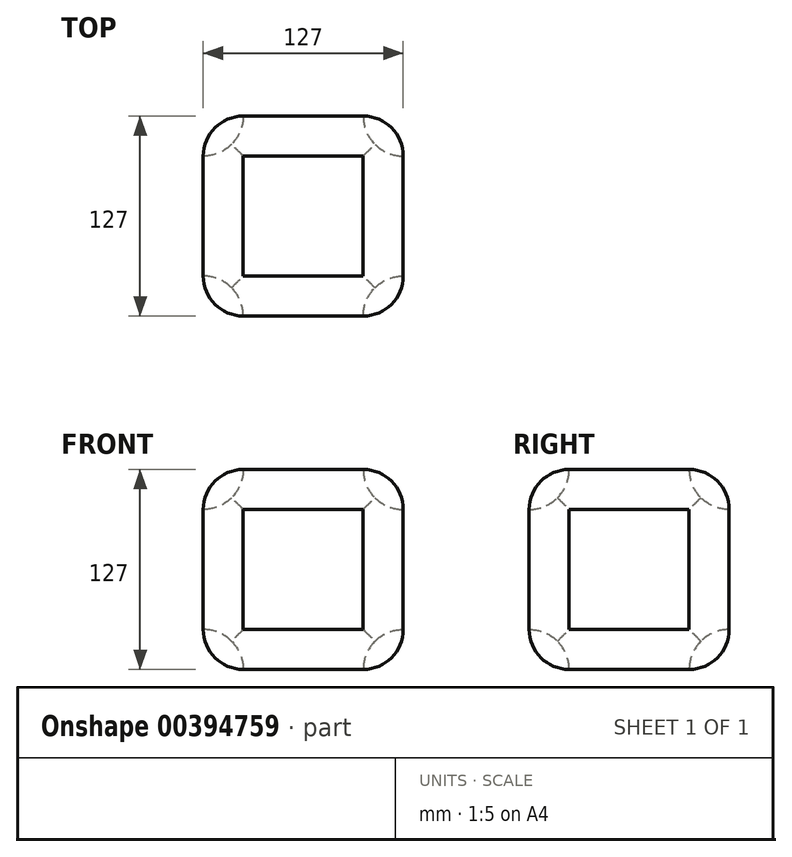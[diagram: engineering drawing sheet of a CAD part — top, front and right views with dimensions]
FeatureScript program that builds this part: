
annotation { "Feature Type Name" : "Feature", "Feature Type Description" : "" }
export const myFeature = defineFeature(function(context is Context, id is Id, definition is map)
    precondition{}
    {
        {
            var Q0;
            Q0=qCreatedBy(makeId("Front.planeOp"),FACE);
            var sketch = newSketch(context, id + "F0", { "sketchPlane" : qUnion([Q0])});
            skLineSegment(sketch, "E0.bottom", {"start": v(0, 0) * mm, "end": v(-127, 0) * mm});
            skLineSegment(sketch, "E0.top", {"start": v(0, -127) * mm, "end": v(-127, -127) * mm});
            skLineSegment(sketch, "E0.left", {"start": v(0, 0) * mm, "end": v(0, -127) * mm});
            skLineSegment(sketch, "E0.right", {"start": v(-127, 0) * mm, "end": v(-127, -127) * mm});
            skSolve(sketch);
        }
        {
            var Q0;
            Q0=makeQuery(id+"F0.imprint","IMPRINT",FACE,{"disambiguationData":[TD([[makeQuery(id+"F0.imprint","IMPRINT",EDGE,{"derivedFrom":sQuery(id+"F0.wireOp",EDGE,"E0.bottom")}),1.0]])]});
            extrude(context, id + "F1", {"entities" : qUnion([Q0]), "depth" : 127 * mm});
        }
        {
            var Q0;
            Q0=makeQuery(id+"F1.opExtrude","CAP_FACE",FACE,{"disambiguationData":[OSD([sQuery(id+"F0.wireOp",EDGE,"E0.bottom"),sQuery(id+"F0.wireOp",EDGE,"E0.top"),sQuery(id+"F0.wireOp",EDGE,"E0.left"),sQuery(id+"F0.wireOp",EDGE,"E0.right")])],"isStart":false});
            var sketch = newSketch(context, id + "F2", { "sketchPlane" : qUnion([Q0])});
            skLineSegment(sketch, "E1.bottom", {"start": v(-101.6, -25.4) * mm, "end": v(-25.4, -25.4) * mm});
            skLineSegment(sketch, "E1.top", {"start": v(-101.6, -101.6) * mm, "end": v(-25.4, -101.6) * mm});
            skLineSegment(sketch, "E1.left", {"start": v(-101.6, -25.4) * mm, "end": v(-101.6, -101.6) * mm});
            skLineSegment(sketch, "E1.right", {"start": v(-25.4, -25.4) * mm, "end": v(-25.4, -101.6) * mm});
            skSolve(sketch);
        }
        {
            var Q0;
            Q0=makeQuery(id+"F2.imprint","IMPRINT",FACE,{"disambiguationData":[TD([[makeQuery(id+"F2.imprint","IMPRINT",EDGE,{"derivedFrom":sQuery(id+"F2.wireOp",EDGE,"E1.bottom")}),-1.0]])]});
            var Q1;
            Q1=makeQuery(id+"F1.opExtrude","CAP_FACE",FACE,{"disambiguationData":[OSD([sQuery(id+"F0.wireOp",EDGE,"E0.bottom"),sQuery(id+"F0.wireOp",EDGE,"E0.top"),sQuery(id+"F0.wireOp",EDGE,"E0.left"),sQuery(id+"F0.wireOp",EDGE,"E0.right")])],"isStart":true});
            extrude(context, id + "F3", {"entities" : qUnion([Q0]), "operationType" : NewBodyOperationType.REMOVE, "endBound" : BoundingType.THROUGH_ALL, "oppositeDirection" : true, "endBoundEntityFace" : qUnion([Q1]), "depth" : 50.8 * mm});
        }
        {
            var Q0;
            Q0=makeQuery(id+"F1.opExtrude","SWEPT_FACE",FACE,{"disambiguationData":[OSD([sQuery(id+"F0.wireOp",EDGE,"E0.bottom")])]});
            var sketch = newSketch(context, id + "F4", { "sketchPlane" : qUnion([Q0])});
            skLineSegment(sketch, "E2.bottom", {"start": v(-101.6, -101.6) * mm, "end": v(-25.4, -101.6) * mm});
            skLineSegment(sketch, "E2.top", {"start": v(-101.6, -25.4) * mm, "end": v(-25.4, -25.4) * mm});
            skLineSegment(sketch, "E2.left", {"start": v(-101.6, -101.6) * mm, "end": v(-101.6, -25.4) * mm});
            skLineSegment(sketch, "E2.right", {"start": v(-25.4, -101.6) * mm, "end": v(-25.4, -25.4) * mm});
            skSolve(sketch);
        }
        {
            var Q0;
            Q0=makeQuery(id+"F4.imprint","IMPRINT",FACE,{"disambiguationData":[TD([[makeQuery(id+"F4.imprint","IMPRINT",EDGE,{"derivedFrom":sQuery(id+"F4.wireOp",EDGE,"E2.bottom")}),1.0]])]});
            extrude(context, id + "F5", {"entities" : qUnion([Q0]), "operationType" : NewBodyOperationType.REMOVE, "endBound" : BoundingType.THROUGH_ALL, "oppositeDirection" : true, "depth" : 25.4 * mm});
        }
        {
            var Q0;
            Q0=makeQuery(id+"F1.opExtrude","SWEPT_FACE",FACE,{"disambiguationData":[OSD([sQuery(id+"F0.wireOp",EDGE,"E0.left")])]});
            var sketch = newSketch(context, id + "F6", { "sketchPlane" : qUnion([Q0])});
            skLineSegment(sketch, "E3.bottom", {"start": v(-101.6, -25.4) * mm, "end": v(-25.4, -25.4) * mm});
            skLineSegment(sketch, "E3.top", {"start": v(-101.6, -101.6) * mm, "end": v(-25.4, -101.6) * mm});
            skLineSegment(sketch, "E3.left", {"start": v(-101.6, -25.4) * mm, "end": v(-101.6, -101.6) * mm});
            skLineSegment(sketch, "E3.right", {"start": v(-25.4, -25.4) * mm, "end": v(-25.4, -101.6) * mm});
            skSolve(sketch);
        }
        {
            var Q0;
            Q0=makeQuery(id+"F6.imprint","IMPRINT",FACE,{"disambiguationData":[TD([[makeQuery(id+"F6.imprint","IMPRINT",EDGE,{"derivedFrom":sQuery(id+"F6.wireOp",EDGE,"E3.bottom")}),-1.0]])]});
            extrude(context, id + "F7", {"entities" : qUnion([Q0]), "operationType" : NewBodyOperationType.REMOVE, "endBound" : BoundingType.THROUGH_ALL, "oppositeDirection" : true, "depth" : 25.4 * mm});
        }
        {
            var Q0;
            Q0=makeQuery(id+"F1.opExtrude","CAP_EDGE",EDGE,{"disambiguationData":[OSD([sQuery(id+"F0.wireOp",EDGE,"E0.bottom")])],"isStart":false});
            fillet(context, id + "F8", {"entities" : qUnion([Q0]), "radius" : 25.4 * mm, "tangentPropagation" : true, "allowEdgeOverflow" : false});
        }
        {
            var Q0;
            Q0=makeQuery(id+"F1.opExtrude","SWEPT_EDGE",EDGE,{"disambiguationData":[OSD([sQuery(id+"F0.wireOp",EDGE,"E0.bottom"),sQuery(id+"F0.wireOp",EDGE,"E0.left")])]});
            fillet(context, id + "F9", {"entities" : qUnion([Q0]), "radius" : 25.4 * mm, "tangentPropagation" : true, "allowEdgeOverflow" : false});
        }
        {
            var Q0;
            Q0=makeQuery(id+"F9.opFillet","BLEND_EDGE",EDGE,{"blendedFrom":[makeQuery(id+"F1.opExtrude","CAP_EDGE",EDGE,{"disambiguationData":[OSD([sQuery(id+"F0.wireOp",EDGE,"E0.left")])],"isStart":false}),makeQuery(id+"F1.opExtrude","SWEPT_FACE",FACE,{"disambiguationData":[OSD([sQuery(id+"F0.wireOp",EDGE,"E0.top")])]})],"blendedInto":[makeQuery(id+"F1.opExtrude","SWEPT_FACE",FACE,{"disambiguationData":[OSD([sQuery(id+"F0.wireOp",EDGE,"E0.top")])]})]});
            fillet(context, id + "F10", {"entities" : qUnion([Q0]), "radius" : 25.4 * mm, "tangentPropagation" : true, "allowEdgeOverflow" : false});
        }
        {
            var Q0;
            Q0=makeQuery(id+"F1.opExtrude","CAP_EDGE",EDGE,{"disambiguationData":[OSD([sQuery(id+"F0.wireOp",EDGE,"E0.left")])],"isStart":true});
            fillet(context, id + "F11", {"entities" : qUnion([Q0]), "radius" : 25.4 * mm, "tangentPropagation" : true, "allowEdgeOverflow" : false});
        }
        {
            var Q0;
            Q0=makeQuery(id+"F1.opExtrude","CAP_EDGE",EDGE,{"disambiguationData":[OSD([sQuery(id+"F0.wireOp",EDGE,"E0.right")])],"isStart":false});
            fillet(context, id + "F12", {"entities" : qUnion([Q0]), "radius" : 25.4 * mm, "tangentPropagation" : true, "allowEdgeOverflow" : false});
        }
        {
            var Q0;
            Q0=makeQuery(id+"F7.boolean.opBoolean","INTERSECT",EDGE,{"derivedFrom":[makeQuery(id+"F5.boolean.opBoolean","MERGE",FACE,{"derivedFrom":[makeQuery(id+"F3.boolean.opBoolean","COPY",FACE,{"derivedFrom":makeQuery(id+"F3.opExtrude","SWEPT_FACE",FACE,{"disambiguationData":[OSD([sQuery(id+"F2.wireOp",EDGE,"E1.left")])]})}),makeQuery(id+"F5.opExtrude","SWEPT_FACE",FACE,{"disambiguationData":[OSD([sQuery(id+"F4.wireOp",EDGE,"E2.left")])]})]}),makeQuery(id+"F7.opExtrude","SWEPT_FACE",FACE,{"disambiguationData":[OSD([sQuery(id+"F6.wireOp",EDGE,"E3.bottom")])]})]});
            fillet(context, id + "F13", {"entities" : qUnion([Q0]), "radius" : 25.4 * mm, "tangentPropagation" : true, "allowEdgeOverflow" : false});
        }
        {
            var Q0;
            Q0=makeQuery(id+"F5.boolean.opBoolean","INTERSECT",EDGE,{"derivedFrom":[makeQuery(id+"F3.boolean.opBoolean","COPY",FACE,{"derivedFrom":makeQuery(id+"F3.opExtrude","SWEPT_FACE",FACE,{"disambiguationData":[OSD([sQuery(id+"F2.wireOp",EDGE,"E1.bottom")])]})}),makeQuery(id+"F5.opExtrude","SWEPT_FACE",FACE,{"disambiguationData":[OSD([sQuery(id+"F4.wireOp",EDGE,"E2.top")])]})]});
            fillet(context, id + "F14", {"entities" : qUnion([Q0]), "radius" : 25.4 * mm, "tangentPropagation" : true, "allowEdgeOverflow" : false});
        }
        {
            var Q0;
            Q0=makeQuery(id+"F7.boolean.opBoolean","INTERSECT",EDGE,{"derivedFrom":[makeQuery(id+"F5.boolean.opBoolean","MERGE",FACE,{"derivedFrom":[makeQuery(id+"F3.boolean.opBoolean","COPY",FACE,{"derivedFrom":makeQuery(id+"F3.opExtrude","SWEPT_FACE",FACE,{"disambiguationData":[OSD([sQuery(id+"F2.wireOp",EDGE,"E1.left")])]})}),makeQuery(id+"F5.opExtrude","SWEPT_FACE",FACE,{"disambiguationData":[OSD([sQuery(id+"F4.wireOp",EDGE,"E2.left")])]})]}),makeQuery(id+"F7.opExtrude","SWEPT_FACE",FACE,{"disambiguationData":[OSD([sQuery(id+"F6.wireOp",EDGE,"E3.top")])]})]});
            fillet(context, id + "F15", {"entities" : qUnion([Q0]), "radius" : 25.4 * mm, "tangentPropagation" : true, "allowEdgeOverflow" : false});
        }
        {
            var Q0;
            Q0=makeQuery(id+"F5.boolean.opBoolean","INTERSECT",EDGE,{"derivedFrom":[makeQuery(id+"F3.boolean.opBoolean","COPY",FACE,{"derivedFrom":makeQuery(id+"F3.opExtrude","SWEPT_FACE",FACE,{"disambiguationData":[OSD([sQuery(id+"F2.wireOp",EDGE,"E1.top")])]})}),makeQuery(id+"F5.opExtrude","SWEPT_FACE",FACE,{"disambiguationData":[OSD([sQuery(id+"F4.wireOp",EDGE,"E2.bottom")])]})]});
            fillet(context, id + "F16", {"entities" : qUnion([Q0]), "radius" : 25.4 * mm, "tangentPropagation" : true, "allowEdgeOverflow" : false});
        }
        {
            var Q0;
            Q0=makeQuery(id+"F5.boolean.opBoolean","INTERSECT",EDGE,{"derivedFrom":[makeQuery(id+"F3.boolean.opBoolean","COPY",FACE,{"derivedFrom":makeQuery(id+"F3.opExtrude","SWEPT_FACE",FACE,{"disambiguationData":[OSD([sQuery(id+"F2.wireOp",EDGE,"E1.top")])]})}),makeQuery(id+"F5.opExtrude","SWEPT_FACE",FACE,{"disambiguationData":[OSD([sQuery(id+"F4.wireOp",EDGE,"E2.top")])]})]});
            fillet(context, id + "F17", {"entities" : qUnion([Q0]), "radius" : 25.4 * mm, "tangentPropagation" : true, "allowEdgeOverflow" : false});
        }
        {
            var Q0;
            Q0=makeQuery(id+"F7.boolean.opBoolean","INTERSECT",EDGE,{"derivedFrom":[makeQuery(id+"F5.boolean.opBoolean","MERGE",FACE,{"derivedFrom":[makeQuery(id+"F3.boolean.opBoolean","COPY",FACE,{"derivedFrom":makeQuery(id+"F3.opExtrude","SWEPT_FACE",FACE,{"disambiguationData":[OSD([sQuery(id+"F2.wireOp",EDGE,"E1.right")])]})}),makeQuery(id+"F5.opExtrude","SWEPT_FACE",FACE,{"disambiguationData":[OSD([sQuery(id+"F4.wireOp",EDGE,"E2.right")])]})]}),makeQuery(id+"F7.opExtrude","SWEPT_FACE",FACE,{"disambiguationData":[OSD([sQuery(id+"F6.wireOp",EDGE,"E3.top")])]})]});
            fillet(context, id + "F18", {"entities" : qUnion([Q0]), "radius" : 25.4 * mm, "tangentPropagation" : true, "allowEdgeOverflow" : false});
        }
        {
            var Q0;
            Q0=makeQuery(id+"F7.boolean.opBoolean","INTERSECT",EDGE,{"derivedFrom":[makeQuery(id+"F5.boolean.opBoolean","MERGE",FACE,{"derivedFrom":[makeQuery(id+"F3.boolean.opBoolean","COPY",FACE,{"derivedFrom":makeQuery(id+"F3.opExtrude","SWEPT_FACE",FACE,{"disambiguationData":[OSD([sQuery(id+"F2.wireOp",EDGE,"E1.left")])]})}),makeQuery(id+"F5.opExtrude","SWEPT_FACE",FACE,{"disambiguationData":[OSD([sQuery(id+"F4.wireOp",EDGE,"E2.left")])]})]}),makeQuery(id+"F7.opExtrude","SWEPT_FACE",FACE,{"disambiguationData":[OSD([sQuery(id+"F6.wireOp",EDGE,"E3.right")])]})]});
            fillet(context, id + "F19", {"entities" : qUnion([Q0]), "radius" : 25.4 * mm, "tangentPropagation" : true, "allowEdgeOverflow" : false});
        }
        {
            var Q0;
            Q0=makeQuery(id+"F7.boolean.opBoolean","INTERSECT",EDGE,{"derivedFrom":[makeQuery(id+"F5.boolean.opBoolean","MERGE",FACE,{"derivedFrom":[makeQuery(id+"F3.boolean.opBoolean","COPY",FACE,{"derivedFrom":makeQuery(id+"F3.opExtrude","SWEPT_FACE",FACE,{"disambiguationData":[OSD([sQuery(id+"F2.wireOp",EDGE,"E1.left")])]})}),makeQuery(id+"F5.opExtrude","SWEPT_FACE",FACE,{"disambiguationData":[OSD([sQuery(id+"F4.wireOp",EDGE,"E2.left")])]})]}),makeQuery(id+"F7.opExtrude","SWEPT_FACE",FACE,{"disambiguationData":[OSD([sQuery(id+"F6.wireOp",EDGE,"E3.left")])]})]});
            fillet(context, id + "F20", {"entities" : qUnion([Q0]), "radius" : 25.4 * mm, "tangentPropagation" : true, "allowEdgeOverflow" : false});
        }
        {
            var Q0;
            Q0=makeQuery(id+"F7.boolean.opBoolean","INTERSECT",EDGE,{"derivedFrom":[makeQuery(id+"F5.boolean.opBoolean","MERGE",FACE,{"derivedFrom":[makeQuery(id+"F3.boolean.opBoolean","COPY",FACE,{"derivedFrom":makeQuery(id+"F3.opExtrude","SWEPT_FACE",FACE,{"disambiguationData":[OSD([sQuery(id+"F2.wireOp",EDGE,"E1.right")])]})}),makeQuery(id+"F5.opExtrude","SWEPT_FACE",FACE,{"disambiguationData":[OSD([sQuery(id+"F4.wireOp",EDGE,"E2.right")])]})]}),makeQuery(id+"F7.opExtrude","SWEPT_FACE",FACE,{"disambiguationData":[OSD([sQuery(id+"F6.wireOp",EDGE,"E3.right")])]})]});
            fillet(context, id + "F21", {"entities" : qUnion([Q0]), "radius" : 25.4 * mm, "tangentPropagation" : true, "allowEdgeOverflow" : false});
        }
        {
            var Q0;
            Q0=makeQuery(id+"F7.boolean.opBoolean","INTERSECT",EDGE,{"derivedFrom":[makeQuery(id+"F5.boolean.opBoolean","MERGE",FACE,{"derivedFrom":[makeQuery(id+"F3.boolean.opBoolean","COPY",FACE,{"derivedFrom":makeQuery(id+"F3.opExtrude","SWEPT_FACE",FACE,{"disambiguationData":[OSD([sQuery(id+"F2.wireOp",EDGE,"E1.right")])]})}),makeQuery(id+"F5.opExtrude","SWEPT_FACE",FACE,{"disambiguationData":[OSD([sQuery(id+"F4.wireOp",EDGE,"E2.right")])]})]}),makeQuery(id+"F7.opExtrude","SWEPT_FACE",FACE,{"disambiguationData":[OSD([sQuery(id+"F6.wireOp",EDGE,"E3.left")])]})]});
            fillet(context, id + "F22", {"entities" : qUnion([Q0]), "radius" : 25.4 * mm, "tangentPropagation" : true, "allowEdgeOverflow" : false});
        }
        {
            var Q0;
            Q0=makeQuery(id+"F7.boolean.opBoolean","INTERSECT",EDGE,{"derivedFrom":[makeQuery(id+"F5.boolean.opBoolean","MERGE",FACE,{"derivedFrom":[makeQuery(id+"F3.boolean.opBoolean","COPY",FACE,{"derivedFrom":makeQuery(id+"F3.opExtrude","SWEPT_FACE",FACE,{"disambiguationData":[OSD([sQuery(id+"F2.wireOp",EDGE,"E1.right")])]})}),makeQuery(id+"F5.opExtrude","SWEPT_FACE",FACE,{"disambiguationData":[OSD([sQuery(id+"F4.wireOp",EDGE,"E2.right")])]})]}),makeQuery(id+"F7.opExtrude","SWEPT_FACE",FACE,{"disambiguationData":[OSD([sQuery(id+"F6.wireOp",EDGE,"E3.bottom")])]})]});
            fillet(context, id + "F23", {"entities" : qUnion([Q0]), "radius" : 25.4 * mm, "tangentPropagation" : true, "allowEdgeOverflow" : false});
        }
        {
            var Q0;
            Q0=makeQuery(id+"F5.boolean.opBoolean","INTERSECT",EDGE,{"derivedFrom":[makeQuery(id+"F3.boolean.opBoolean","COPY",FACE,{"derivedFrom":makeQuery(id+"F3.opExtrude","SWEPT_FACE",FACE,{"disambiguationData":[OSD([sQuery(id+"F2.wireOp",EDGE,"E1.bottom")])]})}),makeQuery(id+"F5.opExtrude","SWEPT_FACE",FACE,{"disambiguationData":[OSD([sQuery(id+"F4.wireOp",EDGE,"E2.bottom")])]})]});
            fillet(context, id + "F24", {"entities" : qUnion([Q0]), "radius" : 25.4 * mm, "tangentPropagation" : true, "allowEdgeOverflow" : false});
        }
    });
